# Revit family: Hager-Mini_Gamma-IP30-sistema-NoHosted-CH-it
name_source: partatom
category: Electrical Equipment
units: mm (PartAtom-declared; Revit-internal decimal feet)

## family parameters
Always vertical = Yes
Cut with Voids When Loaded = No
Panel Configuration = Two Columns, Circuits Across
Part Type = Panelboard
Room Calculation Point = No
Round Connector Dimension = Use Diameter
Shared = No
Work Plane-Based = Yes

## types (5) — shared parameters
Default Elevation = 1219 mm
EF000003 - Tipo di montaggio = EV000384 - A parete
EF000007 - colore = EV000202 - bianco
EF000049 - profondità = 82 mm  [stored 0.269029 ft]
EF000116 - numero RAL = 9010
EF000118 - con piastra di montaggio = No
EF000266 - numero di file = 1
EF001062 - esecuzione EMC = No
EF001134 - barra DIN = No
EF001596 - Attacco Lampada = EV000139 - plastica
EF004462 - tipo di chiusura = EV000154 - altri
EF005474 - grado di protezione (IP) = EV006410 - IP30
EF006244 - coperchio/porta trasparente = No
EF006306 - con serratura = No
EF009212 - esecuzione coperchio = EV009916 - con taglio
EF015941 - Segnale di passaggio porta = No
HG000001 - Numero di colonne = 1
HG000002 - Con porta = No
HG000003 - Gamma = Mini gamma
HG000005 - Spessore = 3 mm  [stored 0.00984252 ft]
HG000006 - Ad incasso = No
HG000009 - Porta doppia a battente = No
HG000010 - Porte asimmetriche = No
HG000011 - File vuote nella parte basse = No
HG000017 - Distanza tra i poli = 18 mm  [stored 0.0590551 ft]
Manufacturer = Hager
Type Comments = Mini gamma
zero-valued in all types: EF000218 - profondità di incasso, EF000332 - Altezza della parte incassata, EF000846 - larghezza di montaggio, HG000007 - Numero di colonne vuote, HG000008 - Numero di file vuote

## per-type parameters (varying)
| type | EF000008 - Larghezza | EF000040 - Altezza | EF000339 - tipo di copertura | EF001088 - possibilità di applicazione | EF001131 - profondità interna | EF002950 - Numero moduli DIN | EF015776 - Morsettiera di terra | EF015777 - Morsettiera neutra | HG000004 - Codice produttore | Model |
| A parete IP30 L110 A180 P82 4 Unità di divisione - GD104N | 110 mm | 180 mm | EV001012 - coperchio | No | 0 mm  [stored 0 ft] | 4 | Yes | Yes | GD104N | GD104N |
| A parete IP30 L146 A180 P82 6 Unità di divisione - GD106N | 146 mm | 180 mm | EV005746 - opzionale | Yes | 82 mm  [stored 0.269029 ft] | 6 | Yes | Yes | GD106N | GD106N |
| A parete IP30 L182 A180 P82 8 Unità di divisione - GD108N | 182 mm | 180 mm | EV005746 - opzionale | Yes | 82 mm  [stored 0.269029 ft] | 8 | Yes | Yes | GD108N | GD108N |
| A parete IP30 L218 A180 P82 10 Unità di divisione - GD110N | 218 mm | 180 mm | EV005746 - opzionale | Yes | 82 mm  [stored 0.269029 ft] | 10 | Yes | Yes | GD110N | GD110N |
| A parete IP30 L55 A160 P82 2 Unità di divisione - GD102N | 55 mm  [stored 0.180446 ft] | 160 mm  [stored 0.524934 ft] | EV005746 - opzionale | No | 82 mm  [stored 0.269029 ft] | 2 | No | No | GD102N | GD102N |

note: [stored X ft] marks values corroborated as IEEE doubles in the binary element streams (Revit-internal decimal feet)

## geometry (parser evidence)
native form markers: Sweep x13
no freeform markers — native parametric forms only
